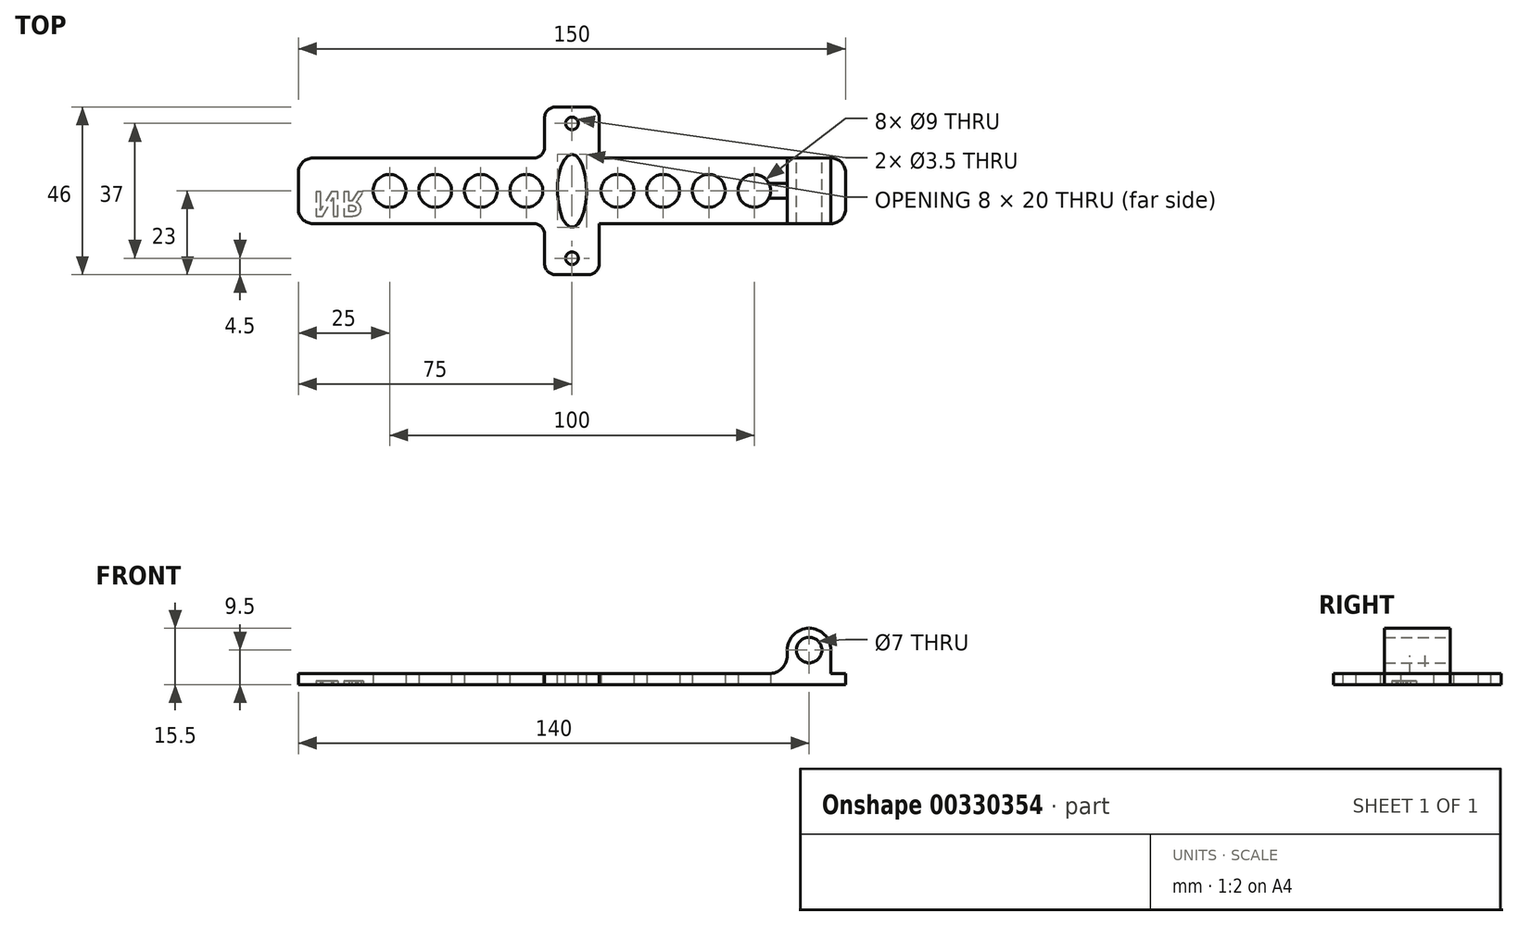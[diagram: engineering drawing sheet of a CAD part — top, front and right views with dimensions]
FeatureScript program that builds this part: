
annotation { "Feature Type Name" : "Feature", "Feature Type Description" : "" }
export const myFeature = defineFeature(function(context is Context, id is Id, definition is map)
    precondition{}
    {
        {
            var Q0;
            Q0=qCreatedBy(makeId("Top.planeOp"),FACE);
            var sketch = newSketch(context, id + "F0", { "sketchPlane" : qUnion([Q0])});
            skLineSegment(sketch, "E0.bottom", {"start": v(-75, 9) * mm, "end": v(75, 9) * mm});
            skLineSegment(sketch, "E0.top", {"start": v(-75, -9) * mm, "end": v(75, -9) * mm});
            skLineSegment(sketch, "E0.left", {"start": v(-75, 9) * mm, "end": v(-75, -9) * mm});
            skLineSegment(sketch, "E0.right", {"start": v(75, 9) * mm, "end": v(75, -9) * mm});
            skPoint(sketch, "E0.middle", {"position": v(0, 0) * mm});
            skPoint(sketch, "E1.middle.positionSnap0", {"position": v(0, 9) * mm});
            skPoint(sketch, "E1.centerSnap0", {"position": v(0, 9) * mm});
            skLineSegment(sketch, "E2.bottom", {"start": v(-7.5, 23) * mm, "end": v(7.5, 23) * mm});
            skLineSegment(sketch, "E2.top", {"start": v(-7.5, -23) * mm, "end": v(7.5, -23) * mm});
            skLineSegment(sketch, "E2.left", {"start": v(-7.5, 23) * mm, "end": v(-7.5, -23) * mm});
            skLineSegment(sketch, "E2.right", {"start": v(7.5, 23) * mm, "end": v(7.5, -23) * mm});
            skLineSegment(sketch, "E3", {"start": v(-82.5, -18.5) * mm, "end": v(82.5, -18.5) * mm, "construction": true});
            skLineSegment(sketch, "E4", {"start": v(-80.75, 18.5) * mm, "end": v(82.5, 18.5) * mm, "construction": true});
            skPoint(sketch, "E5.MirrorCS.end.orphan", {"position": v(-75, -23) * mm});
            skPoint(sketch, "E5.MirrorCS.start.orphan", {"position": v(-90, -23) * mm});
            skPoint(sketch, "E6.orphan", {"position": v(-75, -9) * mm});
            skPoint(sketch, "E7.center.orphan", {"position": v(-82.5, 18.5) * mm});
            skPoint(sketch, "E8.start.orphan", {"position": v(-90, 23) * mm});
            skPoint(sketch, "E9.end.orphan", {"position": v(-75, 23) * mm});
            skPoint(sketch, "E10.MirrorCS.end.orphan", {"position": v(75, 23) * mm});
            skPoint(sketch, "E10.MirrorCS.start.orphan", {"position": v(90, 23) * mm});
            skPoint(sketch, "E11.orphan", {"position": v(75, 9) * mm});
            skPoint(sketch, "E12.MirrorCS.end.orphan", {"position": v(90, -23) * mm});
            skPoint(sketch, "E13.MirrorCS.end.orphan", {"position": v(75, -23) * mm});
            skPoint(sketch, "E14.MirrorCS.start.orphan", {"position": v(75, -9) * mm});
            skSolve(sketch);
        }
        {
            var Q0;
            Q0=makeQuery(id+"F0.imprint","IMPRINT",FACE,{"disambiguationData":[TD([[makeQuery(id+"F0.imprint","IMPRINT",EDGE,{"derivedFrom":sQuery(id+"F0.wireOp",EDGE,"E0.bottom")}),-1.0]])]});
            var Q1;
            Q1=makeQuery(id+"F0.imprint","IMPRINT",FACE,{"disambiguationData":[TD([[makeQuery(id+"F0.imprint","IMPRINT",EDGE,{"derivedFrom":sQuery(id+"F0.wireOp",EDGE,"E0.left")}),-1.0]])]});
            var Q2;
            Q2=makeQuery(id+"F0.imprint","IMPRINT",FACE,{"disambiguationData":[TD([[makeQuery(id+"F0.imprint","IMPRINT",EDGE,{"derivedFrom":sQuery(id+"F0.wireOp",EDGE,"E0.right")}),1.0]])]});
            extrude(context, id + "F1", {"entities" : qUnion([Q0, Q1, Q2]), "endBound" : BoundingType.SYMMETRIC, "depth" : 3 * mm});
        }
        {
            var Q0;
            Q0=makeQuery(id+"F1.opExtrude","SWEPT_FACE",FACE,{"disambiguationData":[OSD([sQuery(id+"F0.wireOp",EDGE,"E0.bottom")])]});
            var sketch = newSketch(context, id + "F2", { "sketchPlane" : qUnion([Q0])});
            skCircle(sketch, "E15", {"center": v(-65, 8) * mm, "radius": 3.5 * mm});
            skArc(sketch, "E16", {"start": v(-59, 8) * mm, "mid": v(-65, 14) * mm, "end": v(-71, 8) * mm});
            skLineSegment(sketch, "E17", {"start": v(-59, 8) * mm, "end": v(-59, 1.5) * mm});
            skLineSegment(sketch, "E18", {"start": v(-71, 1.5) * mm, "end": v(-71, 8) * mm});
            skArc(sketch, "E19.MirrorCS", {"start": v(59, 8) * mm, "mid": v(65, 14) * mm, "end": v(71, 8) * mm});
            skLineSegment(sketch, "E20.MirrorCS", {"start": v(59, 8) * mm, "end": v(59, 1.5) * mm});
            skLineSegment(sketch, "E21.MirrorCS", {"start": v(71, 1.5) * mm, "end": v(71, 8) * mm});
            skCircle(sketch, "E22.MirrorC", {"center": v(65, 8) * mm, "radius": 3.5 * mm});
            skSolve(sketch);
        }
        {
            var Q0;
            Q0=makeQuery(id+"F2.imprint","IMPRINT",FACE,{"disambiguationData":[TD([[makeQuery(id+"F2.imprint","IMPRINT",EDGE,{"derivedFrom":sQuery(id+"F2.wireOp",EDGE,"E15")}),-1.0]])]});
            var Q1;
            Q1=makeQuery(id+"F2.imprint","IMPRINT",FACE,{"disambiguationData":[TD([[makeQuery(id+"F2.imprint","IMPRINT",EDGE,{"derivedFrom":sQuery(id+"F2.wireOp",EDGE,"E19.MirrorCS")}),-1.0]])]});
            extrude(context, id + "F3", {"entities" : qUnion([Q0, Q1]), "operationType" : NewBodyOperationType.ADD, "oppositeDirection" : true, "depth" : 18 * mm});
        }
        {
            var Q0;
            Q0=makeQuery(id+"F1.opExtrude","SWEPT_EDGE",EDGE,{"disambiguationData":[OSD([sQuery(id+"F0.wireOp",EDGE,"E8"),sQuery(id+"F0.wireOp",EDGE,"E9")])]});
            var Q1;
            Q1=makeQuery(id+"F1.opExtrude","SWEPT_EDGE",EDGE,{"disambiguationData":[OSD([sQuery(id+"F0.wireOp",EDGE,"IWv036N6-hER4-TjgN-3p1i-bJgQ2zKYnuwy"),sQuery(id+"F0.wireOp",EDGE,"E8")])]});
            var Q2;
            Q2=makeQuery(id+"F1.opExtrude","SWEPT_EDGE",EDGE,{"disambiguationData":[OSD([sQuery(id+"F0.wireOp",EDGE,"IWv036N6-hER4-TjgN-3p1i-bJgQ2zKYnuwy"),sQuery(id+"F0.wireOp",EDGE,"E5.MirrorCS")])]});
            var Q3;
            Q3=makeQuery(id+"F1.opExtrude","SWEPT_EDGE",EDGE,{"disambiguationData":[OSD([sQuery(id+"F0.wireOp",EDGE,"E5.MirrorCS"),sQuery(id+"F0.wireOp",EDGE,"3aeacbfe-3875-4deb-bdc6-79265fee12740.MirrorCS")])]});
            var Q4;
            Q4=makeQuery(id+"F1.opExtrude","SWEPT_EDGE",EDGE,{"disambiguationData":[OSD([sQuery(id+"F0.wireOp",EDGE,"E12.MirrorCS"),sQuery(id+"F0.wireOp",EDGE,"E10.MirrorCS")])]});
            var Q5;
            Q5=makeQuery(id+"F1.opExtrude","SWEPT_EDGE",EDGE,{"disambiguationData":[OSD([sQuery(id+"F0.wireOp",EDGE,"E10.MirrorCS"),sQuery(id+"F0.wireOp",EDGE,"d51349f5-c044-474a-9672-9cdd4869d1c60.MirrorCS")])]});
            var Q6;
            Q6=makeQuery(id+"F1.opExtrude","SWEPT_EDGE",EDGE,{"disambiguationData":[OSD([sQuery(id+"F0.wireOp",EDGE,"E12.MirrorCS"),sQuery(id+"F0.wireOp",EDGE,"E13.MirrorCS")])]});
            var Q7;
            Q7=makeQuery(id+"F1.opExtrude","SWEPT_EDGE",EDGE,{"disambiguationData":[OSD([sQuery(id+"F0.wireOp",EDGE,"E13.MirrorCS"),sQuery(id+"F0.wireOp",EDGE,"E14.MirrorCS")])]});
            var Q8;
            Q8=makeQuery(id+"F1.opExtrude","SWEPT_EDGE",EDGE,{"disambiguationData":[OSD([sQuery(id+"F0.wireOp",EDGE,"E0.bottom"),sQuery(id+"F0.wireOp",EDGE,"E0.left"),sQuery(id+"F0.wireOp",EDGE,"E9")])]});
            var Q9;
            Q9=makeQuery(id+"F1.opExtrude","SWEPT_EDGE",EDGE,{"disambiguationData":[OSD([sQuery(id+"F0.wireOp",EDGE,"E0.top"),sQuery(id+"F0.wireOp",EDGE,"E0.left"),sQuery(id+"F0.wireOp",EDGE,"3aeacbfe-3875-4deb-bdc6-79265fee12740.MirrorCS")])]});
            var Q10;
            Q10=makeQuery(id+"F1.opExtrude","SWEPT_EDGE",EDGE,{"disambiguationData":[OSD([sQuery(id+"F0.wireOp",EDGE,"E0.top"),sQuery(id+"F0.wireOp",EDGE,"E0.right"),sQuery(id+"F0.wireOp",EDGE,"E14.MirrorCS")])]});
            var Q11;
            Q11=makeQuery(id+"F1.opExtrude","SWEPT_EDGE",EDGE,{"disambiguationData":[OSD([sQuery(id+"F0.wireOp",EDGE,"E0.bottom"),sQuery(id+"F0.wireOp",EDGE,"E0.right"),sQuery(id+"F0.wireOp",EDGE,"d51349f5-c044-474a-9672-9cdd4869d1c60.MirrorCS")])]});
            fillet(context, id + "F4", {"entities" : qUnion([Q0, Q1, Q2, Q3, Q4, Q5, Q6, Q7, Q8, Q9, Q10, Q11]), "radius" : 4 * mm, "tangentPropagation" : true, "allowEdgeOverflow" : false});
        }
        {
            var Q0;
            Q0=makeQuery(id+"F1.opExtrude","CAP_FACE",FACE,{"disambiguationData":[OSD([sQuery(id+"F0.wireOp",EDGE,"E0.bottom"),sQuery(id+"F0.wireOp",EDGE,"E0.top"),sQuery(id+"F0.wireOp",EDGE,"IWv036N6-hER4-TjgN-3p1i-bJgQ2zKYnuwy"),sQuery(id+"F0.wireOp",EDGE,"E7"),sQuery(id+"F0.wireOp",EDGE,"e5306181-353c-4639-a810-9a264477eaa10.MirrorC"),sQuery(id+"F0.wireOp",EDGE,"E8"),sQuery(id+"F0.wireOp",EDGE,"E9"),sQuery(id+"F0.wireOp",EDGE,"E5.MirrorCS"),sQuery(id+"F0.wireOp",EDGE,"3aeacbfe-3875-4deb-bdc6-79265fee12740.MirrorCS"),sQuery(id+"F0.wireOp",EDGE,"E12.MirrorCS"),sQuery(id+"F0.wireOp",EDGE,"E13.MirrorCS"),sQuery(id+"F0.wireOp",EDGE,"2e777d6d-c724-4af3-a05e-c33f32120f4d0.MirrorC"),sQuery(id+"F0.wireOp",EDGE,"272a7535-dd8c-43e2-b832-6a4ce536e0140.MirrorC"),sQuery(id+"F0.wireOp",EDGE,"E10.MirrorCS"),sQuery(id+"F0.wireOp",EDGE,"d51349f5-c044-474a-9672-9cdd4869d1c60.MirrorCS"),sQuery(id+"F0.wireOp",EDGE,"E14.MirrorCS")])],"isStart":true});
            var sketch = newSketch(context, id + "F5", { "sketchPlane" : qUnion([Q0])});
            skCircle(sketch, "E23", {"center": v(-50, 0) * mm, "radius": 4.5 * mm});
            skCircle(sketch, "E24.1.0.0", {"center": v(-37.5, 0) * mm, "radius": 4.5 * mm});
            skCircle(sketch, "E24.2.0.0", {"center": v(-25, 0) * mm, "radius": 4.5 * mm});
            skCircle(sketch, "E24.3.0.0", {"center": v(-12.5, 0) * mm, "radius": 4.5 * mm});
            skCircle(sketch, "E24.5.0.0", {"center": v(12.5, 0) * mm, "radius": 4.5 * mm});
            skCircle(sketch, "E24.6.0.0", {"center": v(25, 0) * mm, "radius": 4.5 * mm});
            skCircle(sketch, "E24.7.0.0", {"center": v(37.5, 0) * mm, "radius": 4.5 * mm});
            skCircle(sketch, "E24.8.0.0", {"center": v(50, 0) * mm, "radius": 4.5 * mm});
            skLineSegment(sketch, "E24.direction1", {"start": v(-50, 0) * mm, "end": v(-37.5, 0) * mm, "construction": true});
            skSolve(sketch);
        }
        {
            var Q0;
            Q0=makeQuery(id+"F5.imprint","IMPRINT",FACE,{"disambiguationData":[TD([[makeQuery(id+"F5.imprint","IMPRINT",EDGE,{"derivedFrom":sQuery(id+"F5.wireOp",EDGE,"E23")}),1.0]])]});
            var Q1;
            Q1=makeQuery(id+"F5.imprint","IMPRINT",FACE,{"disambiguationData":[TD([[makeQuery(id+"F5.imprint","IMPRINT",EDGE,{"derivedFrom":sQuery(id+"F5.wireOp",EDGE,"E24.1.0.0")}),1.0]])]});
            var Q2;
            Q2=makeQuery(id+"F5.imprint","IMPRINT",FACE,{"disambiguationData":[TD([[makeQuery(id+"F5.imprint","IMPRINT",EDGE,{"derivedFrom":sQuery(id+"F5.wireOp",EDGE,"E24.2.0.0")}),1.0]])]});
            var Q3;
            Q3=makeQuery(id+"F5.imprint","IMPRINT",FACE,{"disambiguationData":[TD([[makeQuery(id+"F5.imprint","IMPRINT",EDGE,{"derivedFrom":sQuery(id+"F5.wireOp",EDGE,"E24.3.0.0")}),1.0]])]});
            var Q4;
            Q4=makeQuery(id+"F5.imprint","IMPRINT",FACE,{"disambiguationData":[TD([[makeQuery(id+"F5.imprint","IMPRINT",EDGE,{"derivedFrom":sQuery(id+"F5.wireOp",EDGE,"E24.4.0.0")}),1.0]])]});
            var Q5;
            Q5=makeQuery(id+"F5.imprint","IMPRINT",FACE,{"disambiguationData":[TD([[makeQuery(id+"F5.imprint","IMPRINT",EDGE,{"derivedFrom":sQuery(id+"F5.wireOp",EDGE,"E24.5.0.0")}),1.0]])]});
            var Q6;
            Q6=makeQuery(id+"F5.imprint","IMPRINT",FACE,{"disambiguationData":[TD([[makeQuery(id+"F5.imprint","IMPRINT",EDGE,{"derivedFrom":sQuery(id+"F5.wireOp",EDGE,"E24.6.0.0")}),1.0]])]});
            var Q7;
            Q7=makeQuery(id+"F5.imprint","IMPRINT",FACE,{"disambiguationData":[TD([[makeQuery(id+"F5.imprint","IMPRINT",EDGE,{"derivedFrom":sQuery(id+"F5.wireOp",EDGE,"E24.7.0.0")}),1.0]])]});
            var Q8;
            Q8=makeQuery(id+"F5.imprint","IMPRINT",FACE,{"disambiguationData":[TD([[makeQuery(id+"F5.imprint","IMPRINT",EDGE,{"derivedFrom":sQuery(id+"F5.wireOp",EDGE,"E24.8.0.0")}),1.0]])]});
            var Q9;
            Q9=makeQuery(id+"F5.imprint","IMPRINT",FACE,{"disambiguationData":[TD([[makeQuery(id+"F5.imprint","IMPRINT",EDGE,{"derivedFrom":sQuery(id+"F5.wireOp",EDGE,"El7Yyuof-tK2A-K6ut-bG6y-YLDKy0LXOixn")}),1.0]])]});
            var Q10;
            Q10=makeQuery(id+"F5.imprint","IMPRINT",FACE,{"disambiguationData":[TD([[makeQuery(id+"F5.imprint","IMPRINT",EDGE,{"derivedFrom":sQuery(id+"F5.wireOp",EDGE,"12a1ed7e-ee1c-4fde-bcf8-1ad5c1950c450.MirrorC")}),1.0]])]});
            extrude(context, id + "F6", {"entities" : qUnion([Q0, Q1, Q2, Q3, Q4, Q5, Q6, Q7, Q8, Q9, Q10]), "operationType" : NewBodyOperationType.REMOVE, "endBound" : BoundingType.UP_TO_NEXT, "oppositeDirection" : true, "depth" : 25 * mm});
        }
        {
            var Q0;
            Q0=makeQuery(id+"F3.opExtrude","SWEPT_EDGE",EDGE,{"disambiguationData":[OSD([sQuery(id+"F0.wireOp",EDGE,"E0.bottom"),sQuery(id+"F2.wireOp",EDGE,"E18")])]});
            var Q1;
            Q1=makeQuery(id+"F3.opExtrude","SWEPT_EDGE",EDGE,{"disambiguationData":[OSD([sQuery(id+"F0.wireOp",EDGE,"E0.bottom"),sQuery(id+"F2.wireOp",EDGE,"E17")])]});
            var Q2;
            Q2=makeQuery(id+"F3.opExtrude","SWEPT_EDGE",EDGE,{"disambiguationData":[OSD([sQuery(id+"F0.wireOp",EDGE,"E0.bottom"),sQuery(id+"F2.wireOp",EDGE,"E20.MirrorCS")])]});
            var Q3;
            Q3=makeQuery(id+"F3.opExtrude","SWEPT_EDGE",EDGE,{"disambiguationData":[OSD([sQuery(id+"F0.wireOp",EDGE,"E0.bottom"),sQuery(id+"F2.wireOp",EDGE,"E21.MirrorCS")])]});
            fillet(context, id + "F7", {"entities" : qUnion([Q0, Q1, Q2, Q3]), "radius" : 5 * mm, "tangentPropagation" : true, "allowEdgeOverflow" : false});
        }
        {
            var Q0;
            Q0=makeQuery(id+"F1.opExtrude","CAP_FACE",FACE,{"disambiguationData":[OSD([sQuery(id+"F0.wireOp",EDGE,"E0.bottom"),sQuery(id+"F0.wireOp",EDGE,"E0.top"),sQuery(id+"F0.wireOp",EDGE,"IWv036N6-hER4-TjgN-3p1i-bJgQ2zKYnuwy"),sQuery(id+"F0.wireOp",EDGE,"E7"),sQuery(id+"F0.wireOp",EDGE,"e5306181-353c-4639-a810-9a264477eaa10.MirrorC"),sQuery(id+"F0.wireOp",EDGE,"E8"),sQuery(id+"F0.wireOp",EDGE,"E9"),sQuery(id+"F0.wireOp",EDGE,"E5.MirrorCS"),sQuery(id+"F0.wireOp",EDGE,"3aeacbfe-3875-4deb-bdc6-79265fee12740.MirrorCS"),sQuery(id+"F0.wireOp",EDGE,"E12.MirrorCS"),sQuery(id+"F0.wireOp",EDGE,"E13.MirrorCS"),sQuery(id+"F0.wireOp",EDGE,"2e777d6d-c724-4af3-a05e-c33f32120f4d0.MirrorC"),sQuery(id+"F0.wireOp",EDGE,"272a7535-dd8c-43e2-b832-6a4ce536e0140.MirrorC"),sQuery(id+"F0.wireOp",EDGE,"E10.MirrorCS"),sQuery(id+"F0.wireOp",EDGE,"d51349f5-c044-474a-9672-9cdd4869d1c60.MirrorCS"),sQuery(id+"F0.wireOp",EDGE,"E14.MirrorCS")])],"isStart":true});
            var sketch = newSketch(context, id + "F8", { "sketchPlane" : qUnion([Q0])});
            skLineSegment(sketch, "E25", {"start": v(-75, 0) * mm, "end": v(-75, 7) * mm, "construction": true});
            skLineSegment(sketch, "E26", {"start": v(-75, 7) * mm, "end": v(-71, 7) * mm, "construction": true});
            skLineSegment(sketch, "E27", {"start": v(-71, 7) * mm, "end": v(-71, -7) * mm, "construction": true});
            skText(sketch, "E28", { "text": "NR", "fontName": "OpenSans-Bold.ttf"});
            const initialGuessF8  = {"E28": [-0.071, 0.00023, 1, 0, 0.00677]};
            skSetInitialGuess(sketch, initialGuessF8);
            skSolve(sketch);
        }
        {
            var Q0;
            {var subQ5=sQuery(id+"F0.wireOp",EDGE,"E2.top");Q0=makeQuery(id+"F0.imprint","IMPRINT",FACE,{"disambiguationData":[TD([[makeQuery(id+"F0.imprint","IMPRINT",EDGE,{"derivedFrom":subQ5}),1.0]])]});}
            var Q1;
            {var subQ1=sQuery(id+"F0.wireOp",EDGE,"E2.bottom");Q1=makeQuery(id+"F0.imprint","IMPRINT",FACE,{"disambiguationData":[TD([[makeQuery(id+"F0.imprint","IMPRINT",EDGE,{"derivedFrom":subQ1}),-1.0]])]});}
            extrude(context, id + "F9", {"entities" : qUnion([Q0, Q1]), "operationType" : NewBodyOperationType.ADD, "endBound" : BoundingType.SYMMETRIC, "depth" : 2.5 * mm});
        }
        {
            var Q0;
            {var subQ1=sQuery(id+"F0.wireOp",EDGE,"E2.bottom");Q0=makeQuery(id+"F0.imprint","IMPRINT",FACE,{"disambiguationData":[TD([[makeQuery(id+"F0.imprint","IMPRINT",EDGE,{"derivedFrom":subQ1}),-1.0]])]});}
            var Q1;
            {var subQ5=sQuery(id+"F0.wireOp",EDGE,"E2.top");Q1=makeQuery(id+"F0.imprint","IMPRINT",FACE,{"disambiguationData":[TD([[makeQuery(id+"F0.imprint","IMPRINT",EDGE,{"derivedFrom":subQ5}),1.0]])]});}
            extrude(context, id + "F10", {"entities" : qUnion([Q0, Q1]), "operationType" : NewBodyOperationType.ADD, "endBound" : BoundingType.SYMMETRIC, "depth" : 3 * mm});
        }
        {
            var Q0;
            {var subQ0=sQuery(id+"F0.wireOp",EDGE,"E2.left");var subQ1=sQuery(id+"F0.wireOp",EDGE,"E0.bottom");Q0=makeQuery(id+"F10.boolean.opBoolean","MERGE",EDGE,{"derivedFrom":[makeQuery(id+"F9.opExtrude","SWEPT_EDGE",EDGE,{"disambiguationData":[OSD([subQ1,subQ0])]}),makeQuery(id+"F10.opExtrude","SWEPT_EDGE",EDGE,{"disambiguationData":[OSD([subQ1,subQ0])]})]});}
            var Q1;
            {var subQ0=sQuery(id+"F0.wireOp",EDGE,"E2.left");var subQ1=sQuery(id+"F0.wireOp",EDGE,"E2.bottom");Q1=makeQuery(id+"F10.boolean.opBoolean","MERGE",EDGE,{"derivedFrom":[makeQuery(id+"F9.opExtrude","SWEPT_EDGE",EDGE,{"disambiguationData":[OSD([subQ1,subQ0])]}),makeQuery(id+"F10.opExtrude","SWEPT_EDGE",EDGE,{"disambiguationData":[OSD([subQ1,subQ0])]})]});}
            var Q2;
            {var subQ0=sQuery(id+"F0.wireOp",EDGE,"E2.right");var subQ1=sQuery(id+"F0.wireOp",EDGE,"E2.bottom");Q2=makeQuery(id+"F10.boolean.opBoolean","MERGE",EDGE,{"derivedFrom":[makeQuery(id+"F9.opExtrude","SWEPT_EDGE",EDGE,{"disambiguationData":[OSD([subQ1,subQ0])]}),makeQuery(id+"F10.opExtrude","SWEPT_EDGE",EDGE,{"disambiguationData":[OSD([subQ1,subQ0])]})]});}
            var Q3;
            {var subQ0=sQuery(id+"F0.wireOp",EDGE,"E2.right");var subQ1=sQuery(id+"F0.wireOp",EDGE,"E0.bottom");Q3=makeQuery(id+"F10.boolean.opBoolean","MERGE",EDGE,{"derivedFrom":[makeQuery(id+"F9.opExtrude","SWEPT_EDGE",EDGE,{"disambiguationData":[OSD([subQ1,subQ0])]}),makeQuery(id+"F10.opExtrude","SWEPT_EDGE",EDGE,{"disambiguationData":[OSD([subQ1,subQ0])]})]});}
            var Q4;
            {var subQ0=sQuery(id+"F0.wireOp",EDGE,"E2.right");var subQ1=sQuery(id+"F0.wireOp",EDGE,"E0.top");Q4=makeQuery(id+"F10.boolean.opBoolean","MERGE",EDGE,{"derivedFrom":[makeQuery(id+"F9.opExtrude","SWEPT_EDGE",EDGE,{"disambiguationData":[OSD([subQ1,subQ0])]}),makeQuery(id+"F10.opExtrude","SWEPT_EDGE",EDGE,{"disambiguationData":[OSD([subQ1,subQ0])]})]});}
            var Q5;
            {var subQ0=sQuery(id+"F0.wireOp",EDGE,"E2.right");var subQ1=sQuery(id+"F0.wireOp",EDGE,"E2.top");Q5=makeQuery(id+"F10.boolean.opBoolean","MERGE",EDGE,{"derivedFrom":[makeQuery(id+"F9.opExtrude","SWEPT_EDGE",EDGE,{"disambiguationData":[OSD([subQ1,subQ0])]}),makeQuery(id+"F10.opExtrude","SWEPT_EDGE",EDGE,{"disambiguationData":[OSD([subQ1,subQ0])]})]});}
            var Q6;
            {var subQ0=sQuery(id+"F0.wireOp",EDGE,"E2.left");var subQ1=sQuery(id+"F0.wireOp",EDGE,"E0.top");Q6=makeQuery(id+"F10.boolean.opBoolean","MERGE",EDGE,{"derivedFrom":[makeQuery(id+"F9.opExtrude","SWEPT_EDGE",EDGE,{"disambiguationData":[OSD([subQ1,subQ0])]}),makeQuery(id+"F10.opExtrude","SWEPT_EDGE",EDGE,{"disambiguationData":[OSD([subQ1,subQ0])]})]});}
            var Q7;
            {var subQ0=sQuery(id+"F0.wireOp",EDGE,"E2.left");var subQ1=sQuery(id+"F0.wireOp",EDGE,"E2.top");Q7=makeQuery(id+"F10.boolean.opBoolean","MERGE",EDGE,{"derivedFrom":[makeQuery(id+"F9.opExtrude","SWEPT_EDGE",EDGE,{"disambiguationData":[OSD([subQ1,subQ0])]}),makeQuery(id+"F10.opExtrude","SWEPT_EDGE",EDGE,{"disambiguationData":[OSD([subQ1,subQ0])]})]});}
            fillet(context, id + "F11", {"entities" : qUnion([Q0, Q1, Q2, Q3, Q4, Q5, Q6, Q7]), "radius" : 3 * mm, "tangentPropagation" : true, "allowEdgeOverflow" : false});
        }
        {
            var Q0;
            {var subQ0=sQuery(id+"F0.wireOp",EDGE,"E2.right");var subQ1=sQuery(id+"F0.wireOp",EDGE,"E2.left");var subQ2=sQuery(id+"F0.wireOp",EDGE,"E0.top");var subQ3=sQuery(id+"F0.wireOp",EDGE,"E0.bottom");var subQ5=sQuery(id+"F2.wireOp",EDGE,"E17");Q0=makeQuery(id+"F10.boolean.opBoolean","MERGE",FACE,{"derivedFrom":[makeQuery(id+"F3.boolean.opBoolean","SPLIT",FACE,{"disambiguationData":[TD([makeQuery(id+"F3.opExtrude","SWEPT_FACE",FACE,{"disambiguationData":[OSD([subQ5])]})])],"derivedFrom":makeQuery(id+"F1.opExtrude","CAP_FACE",FACE,{"disambiguationData":[OSD([subQ3,subQ2,sQuery(id+"F0.wireOp",EDGE,"IWv036N6-hER4-TjgN-3p1i-bJgQ2zKYnuwy"),sQuery(id+"F0.wireOp",EDGE,"E7"),sQuery(id+"F0.wireOp",EDGE,"e5306181-353c-4639-a810-9a264477eaa10.MirrorC"),sQuery(id+"F0.wireOp",EDGE,"E8"),sQuery(id+"F0.wireOp",EDGE,"E9"),sQuery(id+"F0.wireOp",EDGE,"E5.MirrorCS"),sQuery(id+"F0.wireOp",EDGE,"3aeacbfe-3875-4deb-bdc6-79265fee12740.MirrorCS"),sQuery(id+"F0.wireOp",EDGE,"E12.MirrorCS"),sQuery(id+"F0.wireOp",EDGE,"E13.MirrorCS"),sQuery(id+"F0.wireOp",EDGE,"2e777d6d-c724-4af3-a05e-c33f32120f4d0.MirrorC"),sQuery(id+"F0.wireOp",EDGE,"272a7535-dd8c-43e2-b832-6a4ce536e0140.MirrorC"),sQuery(id+"F0.wireOp",EDGE,"E10.MirrorCS"),sQuery(id+"F0.wireOp",EDGE,"d51349f5-c044-474a-9672-9cdd4869d1c60.MirrorCS"),sQuery(id+"F0.wireOp",EDGE,"E14.MirrorCS")])],"isStart":false})}),makeQuery(id+"F10.opExtrude","CAP_FACE",FACE,{"disambiguationData":[OSD([subQ3,sQuery(id+"F0.wireOp",EDGE,"E2.bottom"),subQ1,subQ0])],"isStart":false}),makeQuery(id+"F10.opExtrude","CAP_FACE",FACE,{"disambiguationData":[OSD([subQ2,sQuery(id+"F0.wireOp",EDGE,"E2.top"),subQ1,subQ0])],"isStart":false})]});}
            var sketch = newSketch(context, id + "F12", { "sketchPlane" : qUnion([Q0])});
            skLineSegment(sketch, "E29", {"start": v(-16.67, 0) * mm, "end": v(-16.67, 18.5) * mm, "construction": true});
            skLineSegment(sketch, "E30", {"start": v(-16.67, 18.5) * mm, "end": v(23.67, 18.5) * mm, "construction": true});
            skCircle(sketch, "E31", {"center": v(0, 18.5) * mm, "radius": 1.75 * mm});
            skLineSegment(sketch, "E32", {"start": v(-16.67, 0) * mm, "end": v(-16.67, -18.5) * mm, "construction": true});
            skLineSegment(sketch, "E33", {"start": v(-16.67, -18.5) * mm, "end": v(23.68, -18.5) * mm, "construction": true});
            skCircle(sketch, "E34", {"center": v(0, -18.5) * mm, "radius": 1.75 * mm});
            skEllipse(sketch, "E35", {"center": v(0, 0) * mm, "majorRadius": 10 * mm, "minorRadius": 4 * mm, "majorAxis": v(0, 1)});
            skSolve(sketch);
        }
        {
            var Q0;
            Q0 = qSketchRegion(id + "F12", true);
            var Q1;
            {var subQ0=sQuery(id+"F0.wireOp",EDGE,"E2.right");var subQ1=sQuery(id+"F0.wireOp",EDGE,"E2.left");var subQ2=sQuery(id+"F0.wireOp",EDGE,"E0.top");var subQ3=sQuery(id+"F0.wireOp",EDGE,"E0.bottom");Q1=makeQuery(id+"F10.boolean.opBoolean","MERGE",FACE,{"derivedFrom":[makeQuery(id+"F1.opExtrude","CAP_FACE",FACE,{"disambiguationData":[OSD([subQ3,subQ2,sQuery(id+"F0.wireOp",EDGE,"IWv036N6-hER4-TjgN-3p1i-bJgQ2zKYnuwy"),sQuery(id+"F0.wireOp",EDGE,"E7"),sQuery(id+"F0.wireOp",EDGE,"e5306181-353c-4639-a810-9a264477eaa10.MirrorC"),sQuery(id+"F0.wireOp",EDGE,"E8"),sQuery(id+"F0.wireOp",EDGE,"E9"),sQuery(id+"F0.wireOp",EDGE,"E5.MirrorCS"),sQuery(id+"F0.wireOp",EDGE,"3aeacbfe-3875-4deb-bdc6-79265fee12740.MirrorCS"),sQuery(id+"F0.wireOp",EDGE,"E12.MirrorCS"),sQuery(id+"F0.wireOp",EDGE,"E13.MirrorCS"),sQuery(id+"F0.wireOp",EDGE,"2e777d6d-c724-4af3-a05e-c33f32120f4d0.MirrorC"),sQuery(id+"F0.wireOp",EDGE,"272a7535-dd8c-43e2-b832-6a4ce536e0140.MirrorC"),sQuery(id+"F0.wireOp",EDGE,"E10.MirrorCS"),sQuery(id+"F0.wireOp",EDGE,"d51349f5-c044-474a-9672-9cdd4869d1c60.MirrorCS"),sQuery(id+"F0.wireOp",EDGE,"E14.MirrorCS")])],"isStart":true}),makeQuery(id+"F10.opExtrude","CAP_FACE",FACE,{"disambiguationData":[OSD([subQ3,sQuery(id+"F0.wireOp",EDGE,"E2.bottom"),subQ1,subQ0])],"isStart":true}),makeQuery(id+"F10.opExtrude","CAP_FACE",FACE,{"disambiguationData":[OSD([subQ2,sQuery(id+"F0.wireOp",EDGE,"E2.top"),subQ1,subQ0])],"isStart":true})]});}
            extrude(context, id + "F13", {"entities" : qUnion([Q0]), "operationType" : NewBodyOperationType.REMOVE, "endBound" : BoundingType.UP_TO_SURFACE, "oppositeDirection" : true, "endBoundEntityFace" : qUnion([Q1]), "depth" : 25 * mm});
        }
        {
            var Q0;
            Q0 = qSketchRegion(id + "F8", true);
            extrude(context, id + "F14", {"entities" : qUnion([Q0]), "operationType" : NewBodyOperationType.REMOVE, "oppositeDirection" : true, "depth" : 1 * mm});
        }
    });
